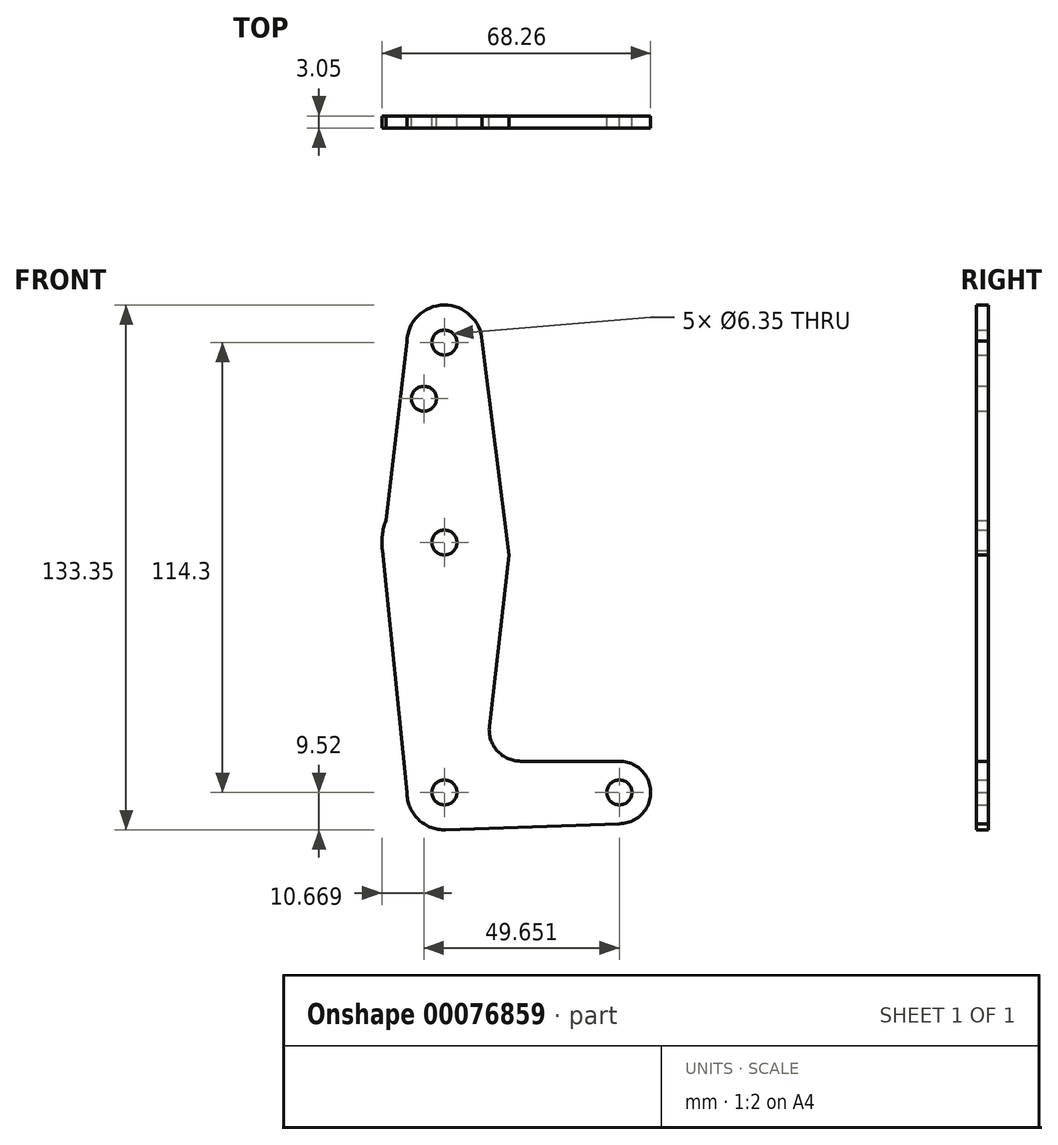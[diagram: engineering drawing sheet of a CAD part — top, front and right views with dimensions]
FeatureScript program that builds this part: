
annotation { "Feature Type Name" : "Feature", "Feature Type Description" : "" }
export const myFeature = defineFeature(function(context is Context, id is Id, definition is map)
    precondition{}
    {
        {
            var Q0;
            Q0=qCreatedBy(makeId("Front.planeOp"),FACE);
            var sketch = newSketch(context, id + "F0", { "sketchPlane" : qUnion([Q0])});
            skLineSegment(sketch, "E0", {"start": v(0, 0) * mm, "end": v(0, 114.3) * mm, "construction": true});
            skLineSegment(sketch, "E1", {"start": v(0, 0) * mm, "end": v(44.45, 0) * mm, "construction": true});
            skCircle(sketch, "E2", {"center": v(0, 0) * mm, "radius": 9.53 * mm});
            skCircle(sketch, "E3", {"center": v(0, 63.5) * mm, "radius": 15.88 * mm});
            skCircle(sketch, "E4", {"center": v(0, 114.3) * mm, "radius": 9.53 * mm});
            skCircle(sketch, "E5", {"center": v(44.45, 0) * mm, "radius": 7.94 * mm});
            skLineSegment(sketch, "E6", {"start": v(-9.52, 0) * mm, "end": v(-15.75, 61.42) * mm});
            skCircle(sketch, "E7", {"center": v(0, 114.3) * mm, "radius": 3.18 * mm});
            skCircle(sketch, "E8", {"center": v(0, 63.5) * mm, "radius": 3.18 * mm});
            skCircle(sketch, "E9", {"center": v(0, 0) * mm, "radius": 3.18 * mm});
            skCircle(sketch, "E10", {"center": v(44.45, 0) * mm, "radius": 3.18 * mm});
            skCircle(sketch, "E11", {"center": v(-5.2, 100.03) * mm, "radius": 3.18 * mm});
            skPoint(sketch, "E12.newPointB", {"position": v(0, 7.93) * mm});
            skLineSegment(sketch, "E13", {"start": v(-9.52, 114.54) * mm, "end": v(-15.75, 61.42) * mm});
            skLineSegment(sketch, "E14", {"start": v(9.52, 114.71) * mm, "end": v(16.41, 60.27) * mm});
            skLineSegment(sketch, "E15", {"start": v(11.44, 16.78) * mm, "end": v(16.41, 60.27) * mm});
            skLineSegment(sketch, "E16", {"start": v(19.34, 7.93) * mm, "end": v(44.45, 7.94) * mm});
            skLineSegment(sketch, "E17", {"start": v(44.45, -7.94) * mm, "end": v(0, -9.53) * mm});
            skArc(sketch, "E18.filletArc", {"start": v(11.44, 16.78) * mm, "mid": v(13.41, 10.59) * mm, "end": v(19.34, 7.93) * mm});
            skSolve(sketch);
        }
        {
            var Q0;
            Q0 = qSketchRegion(id + "F0", true);
            extrude(context, id + "F1", {"entities" : qUnion([Q0]), "depth" : 3.05 * mm});
        }
    });
